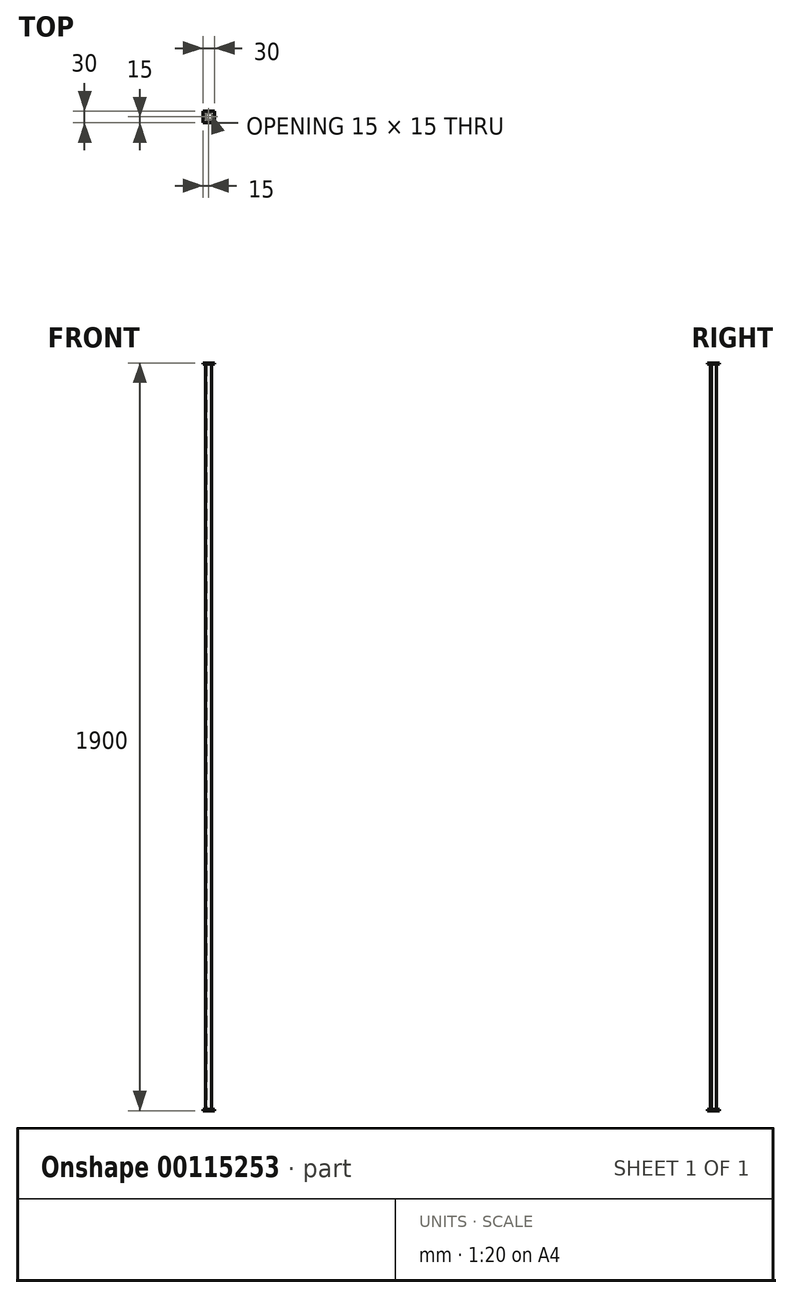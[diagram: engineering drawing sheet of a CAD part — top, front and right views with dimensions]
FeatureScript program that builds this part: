
annotation { "Feature Type Name" : "Feature", "Feature Type Description" : "" }
export const myFeature = defineFeature(function(context is Context, id is Id, definition is map)
    precondition{}
    {
        {
            var Q0;
            Q0=qCreatedBy(makeId("Top.planeOp"),FACE);
            var sketch = newSketch(context, id + "F0", { "sketchPlane" : qUnion([Q0])});
            skLineSegment(sketch, "E0.bottom", {"start": v(0, 0) * mm, "end": v(15, 0) * mm});
            skLineSegment(sketch, "E0.top", {"start": v(0, 15) * mm, "end": v(2, 15) * mm});
            skLineSegment(sketch, "E0.left", {"start": v(0, 0) * mm, "end": v(0, 15) * mm});
            skLineSegment(sketch, "E0.right", {"start": v(15, 0) * mm, "end": v(15, 2) * mm});
            skLineSegment(sketch, "E1.0", {"start": v(2, 2) * mm, "end": v(2, 15) * mm});
            skLineSegment(sketch, "E1.1", {"start": v(2, 2) * mm, "end": v(15, 2) * mm});
            skSolve(sketch);
        }
        {
            var Q0;
            Q0 = qSketchRegion(id + "F0", true);
            extrude(context, id + "F1", {"entities" : qUnion([Q0]), "depth" : (1694 + 200) * mm});
        }
        {
            var Q0;
            Q0=makeQuery(id+"F1.opExtrude","SWEPT_EDGE",EDGE,{"disambiguationData":[OSD([sQuery(id+"F0.wireOp",EDGE,"E1.0"),sQuery(id+"F0.wireOp",EDGE,"E1.1")])]});
            fillet(context, id + "F2", {"entities" : qUnion([Q0]), "radius" : 2 * mm, "tangentPropagation" : true, "allowEdgeOverflow" : false});
        }
        {
            var Q0;
            Q0=makeQuery(id+"F1.opExtrude","SWEPT_EDGE",EDGE,{"disambiguationData":[OSD([sQuery(id+"F0.wireOp",EDGE,"E0.top"),sQuery(id+"F0.wireOp",EDGE,"E1.0")])]});
            var Q1;
            Q1=makeQuery(id+"F1.opExtrude","SWEPT_EDGE",EDGE,{"disambiguationData":[OSD([sQuery(id+"F0.wireOp",EDGE,"E0.right"),sQuery(id+"F0.wireOp",EDGE,"E1.1")])]});
            fillet(context, id + "F3", {"entities" : qUnion([Q0, Q1]), "radius" : 2 * mm, "tangentPropagation" : true, "allowEdgeOverflow" : false});
        }
        {
            var Q0;
            Q0=makeQuery(id+"F1.opExtrude","CAP_FACE",FACE,{"disambiguationData":[OSD([sQuery(id+"F0.wireOp",EDGE,"E0.bottom"),sQuery(id+"F0.wireOp",EDGE,"E0.top"),sQuery(id+"F0.wireOp",EDGE,"E0.left"),sQuery(id+"F0.wireOp",EDGE,"E0.right"),sQuery(id+"F0.wireOp",EDGE,"E1.0"),sQuery(id+"F0.wireOp",EDGE,"E1.1")])],"isStart":false});
            var sketch = newSketch(context, id + "F4", { "sketchPlane" : qUnion([Q0])});
            skLineSegment(sketch, "E2.0", {"start": v(-7.5, 22.5) * mm, "end": v(22.5, 22.5) * mm});
            skLineSegment(sketch, "E2.1", {"start": v(-7.5, -7.5) * mm, "end": v(-7.5, 22.5) * mm});
            skLineSegment(sketch, "E2.2", {"start": v(-7.5, -7.5) * mm, "end": v(22.5, -7.5) * mm});
            skLineSegment(sketch, "E2.3", {"start": v(22.5, -7.5) * mm, "end": v(22.5, 22.5) * mm});
            skLineSegment(sketch, "E3", {"start": v(7.5, 22.5) * mm, "end": v(7.5, -7.5) * mm, "construction": true});
            skLineSegment(sketch, "E4", {"start": v(-7.5, 7.5) * mm, "end": v(22.5, 7.5) * mm, "construction": true});
            skSolve(sketch);
        }
        {
            var Q0;
            Q0 = qSketchRegion(id + "F4", true);
            extrude(context, id + "F5", {"entities" : qUnion([Q0]), "operationType" : NewBodyOperationType.ADD, "depth" : 3 * mm});
        }
        {
            var Q0;
            Q0=makeQuery(id+"F1.opExtrude","CAP_FACE",FACE,{"disambiguationData":[OSD([sQuery(id+"F0.wireOp",EDGE,"E0.bottom"),sQuery(id+"F0.wireOp",EDGE,"E0.top"),sQuery(id+"F0.wireOp",EDGE,"E0.left"),sQuery(id+"F0.wireOp",EDGE,"E0.right"),sQuery(id+"F0.wireOp",EDGE,"E1.0"),sQuery(id+"F0.wireOp",EDGE,"E1.1")])],"isStart":true});
            var sketch = newSketch(context, id + "F6", { "sketchPlane" : qUnion([Q0])});
            skLineSegment(sketch, "E5.0", {"start": v(-7.5, 7.5) * mm, "end": v(22.5, 7.5) * mm});
            skLineSegment(sketch, "E5.1", {"start": v(-7.5, -22.5) * mm, "end": v(-7.5, 7.5) * mm});
            skLineSegment(sketch, "E5.2", {"start": v(-7.5, -22.5) * mm, "end": v(22.5, -22.5) * mm});
            skLineSegment(sketch, "E5.3", {"start": v(22.5, -22.5) * mm, "end": v(22.5, 7.5) * mm});
            skSolve(sketch);
        }
        {
            var Q0;
            Q0 = qSketchRegion(id + "F6", true);
            extrude(context, id + "F7", {"entities" : qUnion([Q0]), "operationType" : NewBodyOperationType.ADD, "depth" : 3 * mm});
        }
    });
